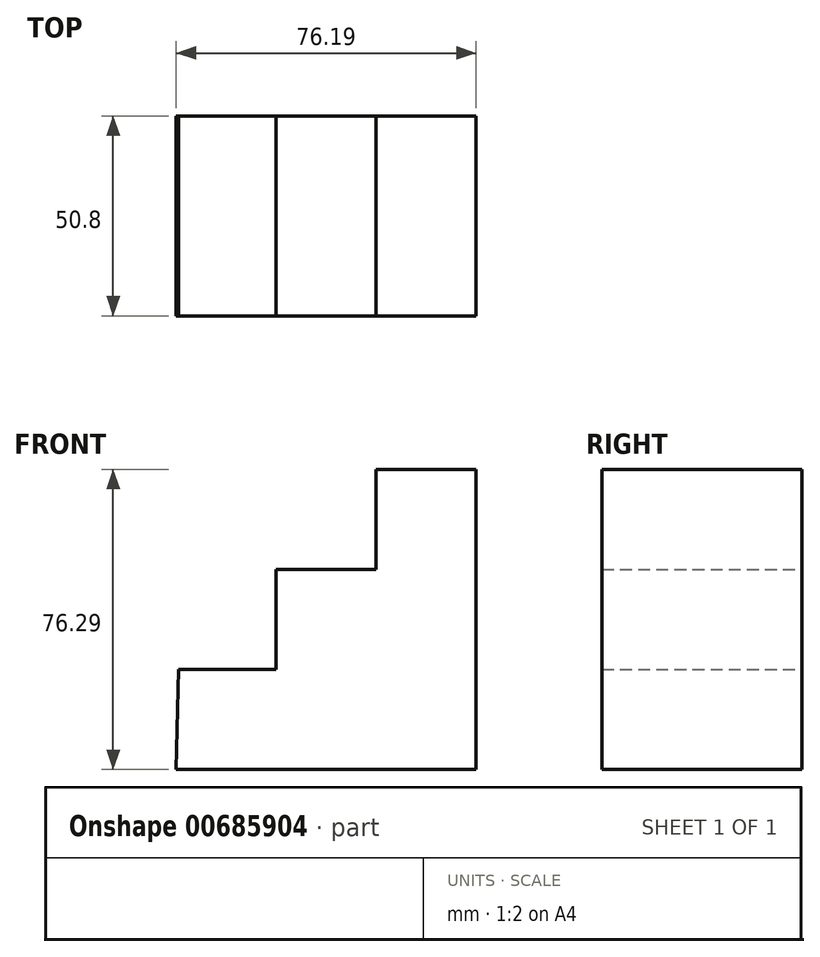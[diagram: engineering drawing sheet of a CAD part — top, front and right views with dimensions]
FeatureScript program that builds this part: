
annotation { "Feature Type Name" : "Feature", "Feature Type Description" : "" }
export const myFeature = defineFeature(function(context is Context, id is Id, definition is map)
    precondition{}
    {
        {
            var Q0;
            Q0=qCreatedBy(makeId("Front.planeOp"),FACE);
            var sketch = newSketch(context, id + "F0", { "sketchPlane" : qUnion([Q0])});
            skLineSegment(sketch, "E0", {"start": v(-46.88, 0) * mm, "end": v(29.31, 0) * mm});
            skLineSegment(sketch, "E1", {"start": v(29.31, 0) * mm, "end": v(29.31, 76.29) * mm});
            skLineSegment(sketch, "E2", {"start": v(29.31, 76.29) * mm, "end": v(3.86, 76.29) * mm});
            skLineSegment(sketch, "E3", {"start": v(3.86, 76.29) * mm, "end": v(3.86, 50.83) * mm});
            skLineSegment(sketch, "E4", {"start": v(3.86, 50.83) * mm, "end": v(-21.58, 50.83) * mm});
            skLineSegment(sketch, "E5", {"start": v(-21.58, 50.83) * mm, "end": v(-21.58, 25.4) * mm});
            skLineSegment(sketch, "E6", {"start": v(-21.58, 25.4) * mm, "end": v(-46.33, 25.4) * mm});
            skLineSegment(sketch, "E7", {"start": v(-46.88, 0) * mm, "end": v(-46.33, 25.4) * mm});
            skSolve(sketch);
        }
        {
            var Q0;
            Q0 = qSketchRegion(id + "F0", true);
            extrude(context, id + "F1", {"entities" : qUnion([Q0]), "depth" : 50.8 * mm, "offsetDistance" : 25.4 * mm});
        }
    });
